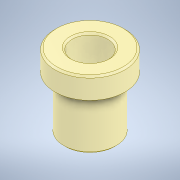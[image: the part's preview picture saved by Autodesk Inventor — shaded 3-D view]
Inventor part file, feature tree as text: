
AUTODESK INVENTOR PART (.ipt)
format: ipt  version: 2022 (Build 260153000, 153)  size: 280,064 bytes
history: native  units: mm
features: extrude x2, sketch x2, chamfer x1, projected_geometry x1
ambient origin geometry x8: Origin, YZ Plane, XZ Plane, XY Plane, X Axis, Y Axis, Z Axis, Center Point
bodies: Solid1 (feature_tree)
feature tree (6):
  extrude  "Extrusion1"  Depth=15.0mm
  extrude  "Extrusion2"  Depth=6.0mm
  chamfer  "Chamfer1"  Distance=6.0mm
  sketch  "Sketch1"  dims[d0=15.0mm d1=10.2mm]
  sketch  "Sketch2"  dims[d2=15.0mm d3=0.0mm d4=20.0mm d5=6.0mm d6=0.0mm d7=0.5mm d8=2.0mm d9=45.0deg d10=0.5mm d11=0.872665mm d12=0.5mm d13=0.872665mm]
  projected_geometry  "Projected Loop1"
